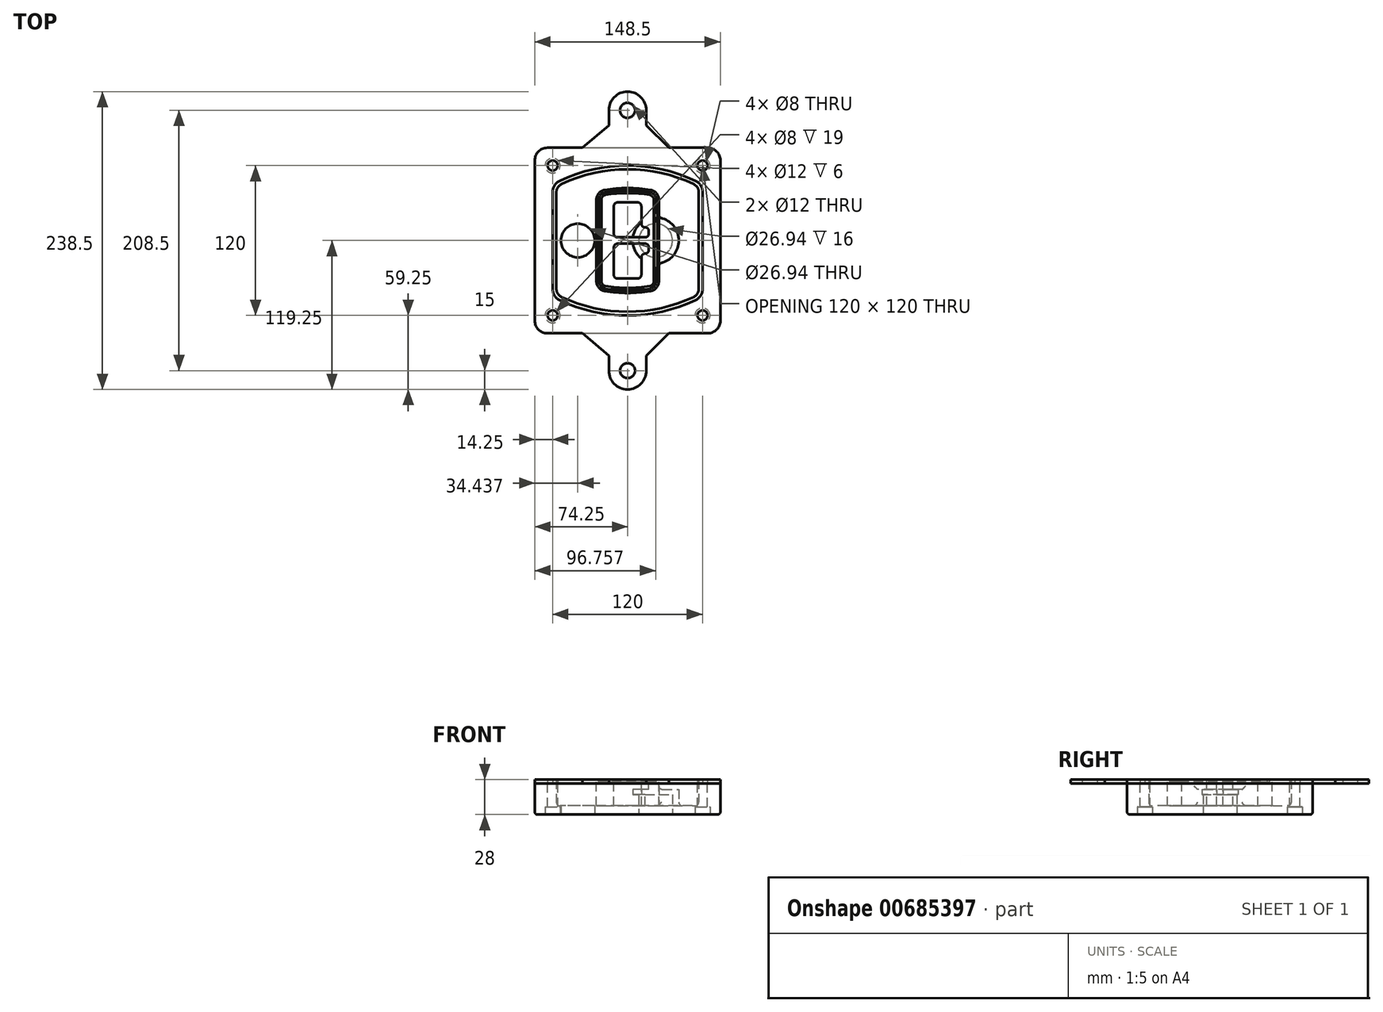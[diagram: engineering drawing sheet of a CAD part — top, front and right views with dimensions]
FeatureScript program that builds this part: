
annotation { "Feature Type Name" : "Feature", "Feature Type Description" : "" }
export const myFeature = defineFeature(function(context is Context, id is Id, definition is map)
    precondition{}
    {
        {
            var Q0;
            Q0=qCreatedBy(makeId("Top.planeOp"),FACE);
            var sketch = newSketch(context, id + "F0", { "sketchPlane" : qUnion([Q0])});
            skPoint(sketch, "E0.rect.middle", {"position": v(0, 0) * mm});
            skLineSegment(sketch, "E1.bottom", {"start": v(-64.25, -74.25) * mm, "end": v(64.25, -74.25) * mm});
            skLineSegment(sketch, "E1.top", {"start": v(-64.25, 74.25) * mm, "end": v(64.25, 74.25) * mm});
            skLineSegment(sketch, "E1.left", {"start": v(-74.25, -64.25) * mm, "end": v(-74.25, 64.25) * mm});
            skLineSegment(sketch, "E1.right", {"start": v(74.25, -64.25) * mm, "end": v(74.25, 64.25) * mm});
            skLineSegment(sketch, "E2", {"start": v(-74.25, 74.25) * mm, "end": v(74.25, -74.25) * mm, "construction": true});
            skLineSegment(sketch, "E3", {"start": v(74.25, 74.25) * mm, "end": v(-74.25, -74.25) * mm, "construction": true});
            skCircle(sketch, "E4", {"center": v(-60, 60) * mm, "radius": 4 * mm});
            skCircle(sketch, "E5", {"center": v(60, 60) * mm, "radius": 4 * mm});
            skCircle(sketch, "E6", {"center": v(60, -60) * mm, "radius": 4 * mm});
            skCircle(sketch, "E7", {"center": v(-60, -60) * mm, "radius": 4 * mm});
            skLineSegment(sketch, "E8", {"start": v(-60, 60) * mm, "end": v(60, 60) * mm, "construction": true});
            skLineSegment(sketch, "E9", {"start": v(60, 60) * mm, "end": v(60, -60) * mm, "construction": true});
            skLineSegment(sketch, "E10", {"start": v(60, -60) * mm, "end": v(-60, -60) * mm, "construction": true});
            skLineSegment(sketch, "E11", {"start": v(-60, -60) * mm, "end": v(-60, 60) * mm, "construction": true});
            skLineSegment(sketch, "E12", {"start": v(-60, 38.83) * mm, "end": v(-60, -38.83) * mm});
            skLineSegment(sketch, "E13", {"start": v(60, 38.83) * mm, "end": v(60, -38.83) * mm});
            skArc(sketch, "E14", {"start": v(54.26, 47.88) * mm, "mid": v(0, 60) * mm, "end": v(-54.26, 47.88) * mm});
            skArc(sketch, "E15", {"start": v(-54.26, -47.88) * mm, "mid": v(0, -60) * mm, "end": v(54.26, -47.88) * mm});
            skLineSegment(sketch, "E16", {"start": v(-60, 0) * mm, "end": v(60, 0) * mm, "construction": true});
            skPoint(sketch, "E17.visualSharp", {"position": v(-60, -45) * mm});
            skArc(sketch, "E17.filletArc", {"start": v(-60, -38.83) * mm, "mid": v(-58.44, -44.2) * mm, "end": v(-54.26, -47.88) * mm});
            skPoint(sketch, "E18.visualSharp", {"position": v(-60, 45) * mm});
            skArc(sketch, "E18.filletArc", {"start": v(-54.26, 47.88) * mm, "mid": v(-58.44, 44.2) * mm, "end": v(-60, 38.83) * mm});
            skPoint(sketch, "E19.visualSharp", {"position": v(60, 45) * mm});
            skArc(sketch, "E19.filletArc", {"start": v(60, 38.83) * mm, "mid": v(58.44, 44.2) * mm, "end": v(54.26, 47.88) * mm});
            skPoint(sketch, "E20.visualSharp", {"position": v(60, -45) * mm});
            skArc(sketch, "E20.filletArc", {"start": v(54.26, -47.88) * mm, "mid": v(58.44, -44.2) * mm, "end": v(60, -38.83) * mm});
            skPoint(sketch, "E21.visualSharp", {"position": v(-74.25, 74.25) * mm});
            skArc(sketch, "E21.filletArc", {"start": v(-64.25, 74.25) * mm, "mid": v(-71.32, 71.32) * mm, "end": v(-74.25, 64.25) * mm});
            skPoint(sketch, "E22.visualSharp", {"position": v(74.25, 74.25) * mm});
            skArc(sketch, "E22.filletArc", {"start": v(74.25, 64.25) * mm, "mid": v(71.32, 71.32) * mm, "end": v(64.25, 74.25) * mm});
            skPoint(sketch, "E23.visualSharp", {"position": v(74.25, -74.25) * mm});
            skArc(sketch, "E23.filletArc", {"start": v(64.25, -74.25) * mm, "mid": v(71.32, -71.32) * mm, "end": v(74.25, -64.25) * mm});
            skPoint(sketch, "E24.visualSharp", {"position": v(-74.25, -74.25) * mm});
            skArc(sketch, "E24.filletArc", {"start": v(-74.25, -64.25) * mm, "mid": v(-71.32, -71.32) * mm, "end": v(-64.25, -74.25) * mm});
            skArc(sketch, "E25.0", {"start": v(57, 38.83) * mm, "mid": v(55.9, 42.58) * mm, "end": v(52.98, 45.17) * mm});
            skLineSegment(sketch, "E25.1", {"start": v(57, 38.83) * mm, "end": v(57, -38.83) * mm});
            skArc(sketch, "E25.2", {"start": v(52.98, -45.17) * mm, "mid": v(55.9, -42.58) * mm, "end": v(57, -38.83) * mm});
            skArc(sketch, "E25.3", {"start": v(-52.98, -45.17) * mm, "mid": v(0, -57) * mm, "end": v(52.98, -45.17) * mm});
            skArc(sketch, "E25.4", {"start": v(-57, -38.83) * mm, "mid": v(-55.9, -42.58) * mm, "end": v(-52.98, -45.17) * mm});
            skArc(sketch, "E25.5", {"start": v(52.98, 45.17) * mm, "mid": v(0, 57) * mm, "end": v(-52.98, 45.17) * mm});
            skLineSegment(sketch, "E25.6", {"start": v(-57, 38.83) * mm, "end": v(-57, -38.83) * mm});
            skArc(sketch, "E25.7", {"start": v(-52.98, 45.17) * mm, "mid": v(-55.9, 42.58) * mm, "end": v(-57, 38.83) * mm});
            skArc(sketch, "E26.0", {"start": v(-55.96, 51.5) * mm, "mid": v(-61.82, 46.33) * mm, "end": v(-64, 38.83) * mm});
            skArc(sketch, "E26.1", {"start": v(55.96, 51.5) * mm, "mid": v(0, 64) * mm, "end": v(-55.96, 51.5) * mm});
            skArc(sketch, "E26.2", {"start": v(64, 38.83) * mm, "mid": v(61.82, 46.33) * mm, "end": v(55.96, 51.5) * mm});
            skLineSegment(sketch, "E26.3", {"start": v(64, 38.83) * mm, "end": v(64, -38.83) * mm});
            skArc(sketch, "E26.4", {"start": v(55.96, -51.5) * mm, "mid": v(61.82, -46.33) * mm, "end": v(64, -38.83) * mm});
            skLineSegment(sketch, "E26.5", {"start": v(-64, 38.83) * mm, "end": v(-64, -38.83) * mm});
            skArc(sketch, "E26.6", {"start": v(-55.96, -51.5) * mm, "mid": v(0, -64) * mm, "end": v(55.96, -51.5) * mm});
            skArc(sketch, "E26.7", {"start": v(-64, -38.83) * mm, "mid": v(-61.82, -46.33) * mm, "end": v(-55.96, -51.5) * mm});
            skSolve(sketch);
        }
        {
            var Q0;
            Q0=makeQuery(id+"F0.imprint","IMPRINT",FACE,{"disambiguationData":[TD([[makeQuery(id+"F0.imprint","IMPRINT",EDGE,{"derivedFrom":sQuery(id+"F0.wireOp",EDGE,"E1.bottom")}),1.0]])]});
            var Q1;
            Q1=makeQuery(id+"F0.imprint","IMPRINT",FACE,{"disambiguationData":[TD([[makeQuery(id+"F0.imprint","IMPRINT",EDGE,{"derivedFrom":sQuery(id+"F0.wireOp",EDGE,"E12")}),1.0]])]});
            var Q2;
            Q2=makeQuery(id+"F0.imprint","IMPRINT",FACE,{"disambiguationData":[TD([[makeQuery(id+"F0.imprint","IMPRINT",EDGE,{"derivedFrom":sQuery(id+"F0.wireOp",EDGE,"E25.0")}),1.0]])]});
            var Q3;
            Q3=makeQuery(id+"F0.imprint","IMPRINT",FACE,{"disambiguationData":[TD([[makeQuery(id+"F0.imprint","IMPRINT",EDGE,{"derivedFrom":sQuery(id+"F0.wireOp",EDGE,"E12")}),-1.0]])]});
            extrude(context, id + "F1", {"entities" : qUnion([Q0, Q1, Q2, Q3]), "oppositeDirection" : true, "depth" : 25 * mm});
        }
        {
            var Q0;
            Q0=makeQuery(id+"F0.imprint","IMPRINT",FACE,{"disambiguationData":[TD([[makeQuery(id+"F0.imprint","IMPRINT",EDGE,{"derivedFrom":sQuery(id+"F0.wireOp",EDGE,"E12")}),1.0]])]});
            extrude(context, id + "F2", {"entities" : qUnion([Q0]), "operationType" : NewBodyOperationType.ADD, "depth" : 3 * mm});
        }
        {
            var Q0;
            Q0=makeQuery(id+"F0.imprint","IMPRINT",FACE,{"disambiguationData":[TD([[makeQuery(id+"F0.imprint","IMPRINT",EDGE,{"derivedFrom":sQuery(id+"F0.wireOp",EDGE,"E25.0")}),1.0]])]});
            extrude(context, id + "F3", {"entities" : qUnion([Q0]), "operationType" : NewBodyOperationType.REMOVE, "oppositeDirection" : true, "depth" : 18 * mm});
        }
        {
            var Q0;
            Q0=makeQuery(id+"F2.opExtrude","CAP_FACE",FACE,{"disambiguationData":[OSD([sQuery(id+"F0.wireOp",EDGE,"E12"),sQuery(id+"F0.wireOp",EDGE,"E13"),sQuery(id+"F0.wireOp",EDGE,"E14"),sQuery(id+"F0.wireOp",EDGE,"E15"),sQuery(id+"F0.wireOp",EDGE,"E17.filletArc"),sQuery(id+"F0.wireOp",EDGE,"E18.filletArc"),sQuery(id+"F0.wireOp",EDGE,"E19.filletArc"),sQuery(id+"F0.wireOp",EDGE,"E20.filletArc"),sQuery(id+"F0.wireOp",EDGE,"E25.0"),sQuery(id+"F0.wireOp",EDGE,"E25.1"),sQuery(id+"F0.wireOp",EDGE,"E25.2"),sQuery(id+"F0.wireOp",EDGE,"E25.3"),sQuery(id+"F0.wireOp",EDGE,"E25.4"),sQuery(id+"F0.wireOp",EDGE,"E25.5"),sQuery(id+"F0.wireOp",EDGE,"E25.6"),sQuery(id+"F0.wireOp",EDGE,"E25.7")])],"isStart":false});
            var sketch = newSketch(context, id + "F4", { "sketchPlane" : qUnion([Q0])});
            skArc(sketch, "E27.0", {"start": v(-18.34, -40.45) * mm, "mid": v(0, -42) * mm, "end": v(18.34, -40.45) * mm});
            skArc(sketch, "E28.0", {"start": v(18.34, 40.45) * mm, "mid": v(0, 42) * mm, "end": v(-18.34, 40.45) * mm});
            skLineSegment(sketch, "E29", {"start": v(-25, 32.57) * mm, "end": v(-25, -32.57) * mm});
            skLineSegment(sketch, "E30", {"start": v(25, 32.57) * mm, "end": v(25, -32.57) * mm});
            skLineSegment(sketch, "E31", {"start": v(-25, 39.1) * mm, "end": v(25, 39.1) * mm, "construction": true});
            skLineSegment(sketch, "E32", {"start": v(-25, -39.1) * mm, "end": v(25, -39.1) * mm, "construction": true});
            skPoint(sketch, "E33.visualSharp", {"position": v(-25, 39.1) * mm});
            skArc(sketch, "E33.filletArc", {"start": v(-18.34, 40.45) * mm, "mid": v(-23.11, 37.73) * mm, "end": v(-25, 32.57) * mm});
            skPoint(sketch, "E34.visualSharp", {"position": v(25, 39.1) * mm});
            skArc(sketch, "E34.filletArc", {"start": v(25, 32.57) * mm, "mid": v(23.11, 37.73) * mm, "end": v(18.34, 40.45) * mm});
            skPoint(sketch, "E35.visualSharp", {"position": v(25, -39.1) * mm});
            skArc(sketch, "E35.filletArc", {"start": v(18.34, -40.45) * mm, "mid": v(23.11, -37.73) * mm, "end": v(25, -32.57) * mm});
            skPoint(sketch, "E36.visualSharp", {"position": v(-25, -39.1) * mm});
            skArc(sketch, "E36.filletArc", {"start": v(-25, -32.57) * mm, "mid": v(-23.11, -37.73) * mm, "end": v(-18.34, -40.45) * mm});
            skArc(sketch, "E37.0", {"start": v(52.98, 45.17) * mm, "mid": v(0, 57) * mm, "end": v(-52.98, 45.17) * mm});
            skArc(sketch, "E37.1", {"start": v(-52.98, 45.17) * mm, "mid": v(-55.9, 42.58) * mm, "end": v(-57, 38.83) * mm});
            skLineSegment(sketch, "E37.2", {"start": v(-57, 38.83) * mm, "end": v(-57, -38.83) * mm});
            skArc(sketch, "E37.3", {"start": v(-57, -38.83) * mm, "mid": v(-55.9, -42.58) * mm, "end": v(-52.98, -45.17) * mm});
            skArc(sketch, "E37.4", {"start": v(-52.98, -45.17) * mm, "mid": v(0, -57) * mm, "end": v(52.98, -45.17) * mm});
            skArc(sketch, "E37.5", {"start": v(52.98, -45.17) * mm, "mid": v(55.9, -42.58) * mm, "end": v(57, -38.83) * mm});
            skLineSegment(sketch, "E37.6", {"start": v(57, 38.83) * mm, "end": v(57, -38.83) * mm});
            skArc(sketch, "E37.7", {"start": v(57, 38.83) * mm, "mid": v(55.9, 42.58) * mm, "end": v(52.98, 45.17) * mm});
            skLineSegment(sketch, "E38.0", {"start": v(23, 32.57) * mm, "end": v(23, -32.57) * mm});
            skArc(sketch, "E38.1", {"start": v(18, -38.48) * mm, "mid": v(21.58, -36.44) * mm, "end": v(23, -32.57) * mm});
            skArc(sketch, "E38.2", {"start": v(-18, -38.48) * mm, "mid": v(0, -40) * mm, "end": v(18, -38.48) * mm});
            skArc(sketch, "E38.3", {"start": v(-23, -32.57) * mm, "mid": v(-21.58, -36.44) * mm, "end": v(-18, -38.48) * mm});
            skLineSegment(sketch, "E38.4", {"start": v(-23, 32.57) * mm, "end": v(-23, -32.57) * mm});
            skArc(sketch, "E38.5", {"start": v(23, 32.57) * mm, "mid": v(21.58, 36.44) * mm, "end": v(18, 38.48) * mm});
            skArc(sketch, "E38.6", {"start": v(-18, 38.48) * mm, "mid": v(-21.58, 36.44) * mm, "end": v(-23, 32.57) * mm});
            skArc(sketch, "E38.7", {"start": v(18, 38.48) * mm, "mid": v(0, 40) * mm, "end": v(-18, 38.48) * mm});
            skArc(sketch, "E39.0", {"start": v(21, 32.57) * mm, "mid": v(20.06, 35.15) * mm, "end": v(17.67, 36.5) * mm});
            skLineSegment(sketch, "E39.1", {"start": v(21, 32.57) * mm, "end": v(21, -32.57) * mm});
            skArc(sketch, "E39.2", {"start": v(17.67, -36.5) * mm, "mid": v(20.06, -35.15) * mm, "end": v(21, -32.57) * mm});
            skArc(sketch, "E39.3", {"start": v(-17.67, -36.5) * mm, "mid": v(0, -38) * mm, "end": v(17.67, -36.5) * mm});
            skArc(sketch, "E39.4", {"start": v(-21, -32.57) * mm, "mid": v(-20.06, -35.15) * mm, "end": v(-17.67, -36.5) * mm});
            skArc(sketch, "E39.5", {"start": v(17.67, 36.5) * mm, "mid": v(0, 38) * mm, "end": v(-17.67, 36.5) * mm});
            skLineSegment(sketch, "E39.6", {"start": v(-21, 32.57) * mm, "end": v(-21, -32.57) * mm});
            skArc(sketch, "E39.7", {"start": v(-17.67, 36.5) * mm, "mid": v(-20.06, 35.15) * mm, "end": v(-21, 32.57) * mm});
            skLineSegment(sketch, "E40", {"start": v(-25, 0) * mm, "end": v(25, 0) * mm, "construction": true});
            skLineSegment(sketch, "E41", {"start": v(-11, 5.5) * mm, "end": v(-11, 27.5) * mm});
            skLineSegment(sketch, "E42", {"start": v(-8, 30.5) * mm, "end": v(8, 30.5) * mm});
            skLineSegment(sketch, "E43", {"start": v(11, 27.5) * mm, "end": v(11, 13.5) * mm});
            skLineSegment(sketch, "E44", {"start": v(14, 10.5) * mm, "end": v(14, 10.5) * mm});
            skLineSegment(sketch, "E45", {"start": v(17, 7.5) * mm, "end": v(17, 5.5) * mm});
            skLineSegment(sketch, "E46", {"start": v(14, 2.5) * mm, "end": v(-8, 2.5) * mm});
            skPoint(sketch, "E47.visualSharp", {"position": v(-11, 30.5) * mm});
            skArc(sketch, "E47.filletArc", {"start": v(-8, 30.5) * mm, "mid": v(-10.12, 29.62) * mm, "end": v(-11, 27.5) * mm});
            skPoint(sketch, "E48.visualSharp", {"position": v(11, 30.5) * mm});
            skArc(sketch, "E48.filletArc", {"start": v(11, 27.5) * mm, "mid": v(10.12, 29.62) * mm, "end": v(8, 30.5) * mm});
            skPoint(sketch, "E49.visualSharp", {"position": v(11, 10.5) * mm});
            skArc(sketch, "E49.filletArc", {"start": v(11, 13.5) * mm, "mid": v(11.88, 11.38) * mm, "end": v(14, 10.5) * mm});
            skPoint(sketch, "E50.visualSharp", {"position": v(17, 10.5) * mm});
            skArc(sketch, "E50.filletArc", {"start": v(17, 7.5) * mm, "mid": v(16.12, 9.62) * mm, "end": v(14, 10.5) * mm});
            skPoint(sketch, "E51.visualSharp", {"position": v(17, 2.5) * mm});
            skArc(sketch, "E51.filletArc", {"start": v(14, 2.5) * mm, "mid": v(16.12, 3.38) * mm, "end": v(17, 5.5) * mm});
            skPoint(sketch, "E52.visualSharp", {"position": v(-11, 2.5) * mm});
            skArc(sketch, "E52.filletArc", {"start": v(-11, 5.5) * mm, "mid": v(-10.12, 3.38) * mm, "end": v(-8, 2.5) * mm});
            skLineSegment(sketch, "E53.0.MirrorCS", {"start": v(14, -2.5) * mm, "end": v(-8, -2.5) * mm});
            skArc(sketch, "E54.0.MirrorCS", {"start": v(-11, -5.5) * mm, "mid": v(-10.12, -3.38) * mm, "end": v(-8, -2.5) * mm});
            skLineSegment(sketch, "E55.0.MirrorCS", {"start": v(-11, -5.5) * mm, "end": v(-11, -27.5) * mm});
            skArc(sketch, "E56.0.MirrorCS", {"start": v(-8, -30.5) * mm, "mid": v(-10.12, -29.62) * mm, "end": v(-11, -27.5) * mm});
            skLineSegment(sketch, "E57.0.MirrorCS", {"start": v(-8, -30.5) * mm, "end": v(8, -30.5) * mm});
            skArc(sketch, "E58.0.MirrorCS", {"start": v(11, -27.5) * mm, "mid": v(10.12, -29.62) * mm, "end": v(8, -30.5) * mm});
            skLineSegment(sketch, "E59.0.MirrorCS", {"start": v(11, -27.5) * mm, "end": v(11, -13.5) * mm});
            skArc(sketch, "E60.0.MirrorCS", {"start": v(11, -13.5) * mm, "mid": v(11.88, -11.38) * mm, "end": v(14, -10.5) * mm});
            skArc(sketch, "E61.0.MirrorCS", {"start": v(17, -7.5) * mm, "mid": v(16.12, -9.62) * mm, "end": v(14, -10.5) * mm});
            skLineSegment(sketch, "E62.0.MirrorCS", {"start": v(17, -7.5) * mm, "end": v(17, -5.5) * mm});
            skArc(sketch, "E63.0.MirrorCS", {"start": v(14, -2.5) * mm, "mid": v(16.12, -3.38) * mm, "end": v(17, -5.5) * mm});
            skSolve(sketch);
        }
        {
            var Q0;
            Q0=makeQuery(id+"F4.imprint","IMPRINT",FACE,{"disambiguationData":[TD([[makeQuery(id+"F4.imprint","IMPRINT",EDGE,{"derivedFrom":sQuery(id+"F4.wireOp",EDGE,"E27.0")}),1.0]])]});
            var Q1;
            Q1=makeQuery(id+"F4.imprint","IMPRINT",FACE,{"disambiguationData":[TD([[makeQuery(id+"F4.imprint","IMPRINT",EDGE,{"derivedFrom":sQuery(id+"F4.wireOp",EDGE,"E38.0")}),-1.0]])]});
            var Q2;
            Q2=makeQuery(id+"F4.imprint","IMPRINT",FACE,{"disambiguationData":[TD([[makeQuery(id+"F4.imprint","IMPRINT",EDGE,{"derivedFrom":sQuery(id+"F4.wireOp",EDGE,"E39.0")}),1.0]])]});
            extrude(context, id + "F5", {"entities" : qUnion([Q0, Q1, Q2]), "operationType" : NewBodyOperationType.ADD, "endBound" : BoundingType.UP_TO_NEXT, "oppositeDirection" : true, "depth" : 25 * mm});
        }
        {
            var Q0;
            Q0=makeQuery(id+"F4.imprint","IMPRINT",FACE,{"disambiguationData":[TD([[makeQuery(id+"F4.imprint","IMPRINT",EDGE,{"derivedFrom":sQuery(id+"F4.wireOp",EDGE,"E38.0")}),-1.0]])]});
            extrude(context, id + "F6", {"entities" : qUnion([Q0]), "operationType" : NewBodyOperationType.REMOVE, "oppositeDirection" : true, "depth" : 2 * mm});
        }
        {
            var Q0;
            Q0=makeQuery(id+"F1.opExtrude","CAP_FACE",FACE,{"disambiguationData":[OSD([sQuery(id+"F0.wireOp",EDGE,"E1.bottom"),sQuery(id+"F0.wireOp",EDGE,"E1.top"),sQuery(id+"F0.wireOp",EDGE,"E1.left"),sQuery(id+"F0.wireOp",EDGE,"E1.right"),sQuery(id+"F0.wireOp",EDGE,"E4"),sQuery(id+"F0.wireOp",EDGE,"E5"),sQuery(id+"F0.wireOp",EDGE,"E6"),sQuery(id+"F0.wireOp",EDGE,"E7"),sQuery(id+"F0.wireOp",EDGE,"E21.filletArc"),sQuery(id+"F0.wireOp",EDGE,"E22.filletArc"),sQuery(id+"F0.wireOp",EDGE,"E23.filletArc"),sQuery(id+"F0.wireOp",EDGE,"E24.filletArc")])],"isStart":false});
            var sketch = newSketch(context, id + "F7", { "sketchPlane" : qUnion([Q0])});
            skCircle(sketch, "E64", {"center": v(22.5, 0) * mm, "radius": 13.47 * mm});
            skCircle(sketch, "E65", {"center": v(-39.81, 0) * mm, "radius": 13.47 * mm});
            skLineSegment(sketch, "E66", {"start": v(74.25, 0) * mm, "end": v(-74.25, 0) * mm});
            skCircle(sketch, "E67", {"center": v(22.5, 0) * mm, "radius": 18.47 * mm});
            skCircle(sketch, "E68", {"center": v(60, -60) * mm, "radius": 6 * mm});
            skCircle(sketch, "E69", {"center": v(-60, -60) * mm, "radius": 6 * mm});
            skCircle(sketch, "E70", {"center": v(-60, 60) * mm, "radius": 6 * mm});
            skCircle(sketch, "E71", {"center": v(60, 60) * mm, "radius": 6 * mm});
            skSolve(sketch);
        }
        {
            var Q0;
            {var subQ1=sQuery(id+"F7.wireOp",EDGE,"E66");var subQ4=sQuery(id+"F7.wireOp",EDGE,"E64");var subQ6=makeQuery(id+"F7.imprint","INTERSECT",VERTEX,{"disambiguationData":[OD(0.0)],"derivedFrom":[subQ4,subQ1]});Q0=makeQuery(id+"F7.imprint","IMPRINT",FACE,{"disambiguationData":[TD([[makeQuery(id+"F7.imprint","IMPRINT",EDGE,{"disambiguationData":[TD([[subQ6,-1.0]])],"derivedFrom":subQ4}),-1.0]])]});}
            var Q1;
            {var subQ0=sQuery(id+"F7.wireOp",EDGE,"E66");var subQ1=sQuery(id+"F7.wireOp",EDGE,"E64");var subQ3=makeQuery(id+"F7.imprint","INTERSECT",VERTEX,{"disambiguationData":[OD(0.0)],"derivedFrom":[subQ1,subQ0]});Q1=makeQuery(id+"F7.imprint","IMPRINT",FACE,{"disambiguationData":[TD([[makeQuery(id+"F7.imprint","IMPRINT",EDGE,{"disambiguationData":[TD([[subQ3,-1.0]])],"derivedFrom":subQ1}),1.0]])]});}
            var Q2;
            {var subQ0=sQuery(id+"F7.wireOp",EDGE,"E66");var subQ1=sQuery(id+"F7.wireOp",EDGE,"E64");var subQ3=makeQuery(id+"F7.imprint","INTERSECT",VERTEX,{"disambiguationData":[OD(0.0)],"derivedFrom":[subQ1,subQ0]});Q2=makeQuery(id+"F7.imprint","IMPRINT",FACE,{"disambiguationData":[TD([[makeQuery(id+"F7.imprint","IMPRINT",EDGE,{"disambiguationData":[TD([[subQ3,1.0]])],"derivedFrom":subQ1}),1.0]])]});}
            var Q3;
            {var subQ1=sQuery(id+"F7.wireOp",EDGE,"E66");var subQ4=sQuery(id+"F7.wireOp",EDGE,"E64");var subQ6=makeQuery(id+"F7.imprint","INTERSECT",VERTEX,{"disambiguationData":[OD(0.0)],"derivedFrom":[subQ4,subQ1]});Q3=makeQuery(id+"F7.imprint","IMPRINT",FACE,{"disambiguationData":[TD([[makeQuery(id+"F7.imprint","IMPRINT",EDGE,{"disambiguationData":[TD([[subQ6,1.0]])],"derivedFrom":subQ4}),-1.0]])]});}
            extrude(context, id + "F8", {"entities" : qUnion([Q0, Q1, Q2, Q3]), "operationType" : NewBodyOperationType.ADD, "oppositeDirection" : true, "depth" : 20 * mm});
        }
        {
            var Q0;
            {var subQ0=sQuery(id+"F7.wireOp",EDGE,"E66");var subQ1=sQuery(id+"F7.wireOp",EDGE,"E64");var subQ3=makeQuery(id+"F7.imprint","INTERSECT",VERTEX,{"disambiguationData":[OD(0.0)],"derivedFrom":[subQ1,subQ0]});Q0=makeQuery(id+"F7.imprint","IMPRINT",FACE,{"disambiguationData":[TD([[makeQuery(id+"F7.imprint","IMPRINT",EDGE,{"disambiguationData":[TD([[subQ3,-1.0]])],"derivedFrom":subQ1}),1.0]])]});}
            var Q1;
            {var subQ0=sQuery(id+"F7.wireOp",EDGE,"E66");var subQ1=sQuery(id+"F7.wireOp",EDGE,"E64");var subQ3=makeQuery(id+"F7.imprint","INTERSECT",VERTEX,{"disambiguationData":[OD(0.0)],"derivedFrom":[subQ1,subQ0]});Q1=makeQuery(id+"F7.imprint","IMPRINT",FACE,{"disambiguationData":[TD([[makeQuery(id+"F7.imprint","IMPRINT",EDGE,{"disambiguationData":[TD([[subQ3,1.0]])],"derivedFrom":subQ1}),1.0]])]});}
            extrude(context, id + "F9", {"entities" : qUnion([Q0, Q1]), "operationType" : NewBodyOperationType.REMOVE, "oppositeDirection" : true, "depth" : 16 * mm});
        }
        {
            var Q0;
            {var subQ0=sQuery(id+"F7.wireOp",EDGE,"E66");var subQ1=sQuery(id+"F7.wireOp",EDGE,"E65");var subQ3=makeQuery(id+"F7.imprint","INTERSECT",VERTEX,{"disambiguationData":[OD(0.0)],"derivedFrom":[subQ1,subQ0]});Q0=makeQuery(id+"F7.imprint","IMPRINT",FACE,{"disambiguationData":[TD([[makeQuery(id+"F7.imprint","IMPRINT",EDGE,{"disambiguationData":[TD([[subQ3,-1.0]])],"derivedFrom":subQ1}),1.0]])]});}
            var Q1;
            {var subQ0=sQuery(id+"F7.wireOp",EDGE,"E66");var subQ1=sQuery(id+"F7.wireOp",EDGE,"E65");var subQ3=makeQuery(id+"F7.imprint","INTERSECT",VERTEX,{"disambiguationData":[OD(0.0)],"derivedFrom":[subQ1,subQ0]});Q1=makeQuery(id+"F7.imprint","IMPRINT",FACE,{"disambiguationData":[TD([[makeQuery(id+"F7.imprint","IMPRINT",EDGE,{"disambiguationData":[TD([[subQ3,1.0]])],"derivedFrom":subQ1}),1.0]])]});}
            extrude(context, id + "F10", {"entities" : qUnion([Q0, Q1]), "operationType" : NewBodyOperationType.REMOVE, "oppositeDirection" : true, "depth" : 25 * mm});
        }
        {
            var Q0;
            Q0=makeQuery(id+"F7.imprint","IMPRINT",FACE,{"disambiguationData":[TD([[makeQuery(id+"F7.imprint","IMPRINT",EDGE,{"derivedFrom":sQuery(id+"F7.wireOp",EDGE,"E68")}),1.0]])]});
            var Q1;
            Q1=makeQuery(id+"F7.imprint","IMPRINT",FACE,{"disambiguationData":[TD([[makeQuery(id+"F7.imprint","IMPRINT",EDGE,{"derivedFrom":makeQuery(id+"F1.opExtrude","CAP_EDGE",EDGE,{"disambiguationData":[OSD([sQuery(id+"F0.wireOp",EDGE,"E5")])],"isStart":false})}),-1.0]])]});
            var Q2;
            Q2=makeQuery(id+"F7.imprint","IMPRINT",FACE,{"disambiguationData":[TD([[makeQuery(id+"F7.imprint","IMPRINT",EDGE,{"derivedFrom":sQuery(id+"F7.wireOp",EDGE,"E69")}),1.0]])]});
            var Q3;
            Q3=makeQuery(id+"F7.imprint","IMPRINT",FACE,{"disambiguationData":[TD([[makeQuery(id+"F7.imprint","IMPRINT",EDGE,{"derivedFrom":makeQuery(id+"F1.opExtrude","CAP_EDGE",EDGE,{"disambiguationData":[OSD([sQuery(id+"F0.wireOp",EDGE,"E4")])],"isStart":false})}),-1.0]])]});
            var Q4;
            Q4=makeQuery(id+"F7.imprint","IMPRINT",FACE,{"disambiguationData":[TD([[makeQuery(id+"F7.imprint","IMPRINT",EDGE,{"derivedFrom":sQuery(id+"F7.wireOp",EDGE,"E70")}),1.0]])]});
            var Q5;
            Q5=makeQuery(id+"F7.imprint","IMPRINT",FACE,{"disambiguationData":[TD([[makeQuery(id+"F7.imprint","IMPRINT",EDGE,{"derivedFrom":makeQuery(id+"F1.opExtrude","CAP_EDGE",EDGE,{"disambiguationData":[OSD([sQuery(id+"F0.wireOp",EDGE,"E7")])],"isStart":false})}),-1.0]])]});
            var Q6;
            Q6=makeQuery(id+"F7.imprint","IMPRINT",FACE,{"disambiguationData":[TD([[makeQuery(id+"F7.imprint","IMPRINT",EDGE,{"derivedFrom":sQuery(id+"F7.wireOp",EDGE,"E71")}),1.0]])]});
            var Q7;
            Q7=makeQuery(id+"F7.imprint","IMPRINT",FACE,{"disambiguationData":[TD([[makeQuery(id+"F7.imprint","IMPRINT",EDGE,{"derivedFrom":makeQuery(id+"F1.opExtrude","CAP_EDGE",EDGE,{"disambiguationData":[OSD([sQuery(id+"F0.wireOp",EDGE,"E6")])],"isStart":false})}),-1.0]])]});
            extrude(context, id + "F11", {"entities" : qUnion([Q0, Q1, Q2, Q3, Q4, Q5, Q6, Q7]), "operationType" : NewBodyOperationType.REMOVE, "oppositeDirection" : true, "depth" : 6 * mm});
        }
        {
            var Q0;
            Q0=makeQuery(id+"F9.boolean.opBoolean","COPY",FACE,{"derivedFrom":makeQuery(id+"F9.opExtrude","CAP_FACE",FACE,{"disambiguationData":[OSD([sQuery(id+"F7.wireOp",EDGE,"E64")])],"isStart":false})});
            var sketch = newSketch(context, id + "F12", { "sketchPlane" : qUnion([Q0])});
            skArc(sketch, "E72.0", {"start": v(11, 14.45) * mm, "mid": v(6.45, 9.13) * mm, "end": v(4.2, 2.5) * mm});
            skArc(sketch, "E72.1", {"start": v(4.2, -2.5) * mm, "mid": v(6.45, -9.13) * mm, "end": v(11, -14.45) * mm});
            skLineSegment(sketch, "E73", {"start": v(4.2, -2.5) * mm, "end": v(14, -2.5) * mm});
            skLineSegment(sketch, "E74.0", {"start": v(14, 2.5) * mm, "end": v(4.2, 2.5) * mm});
            skArc(sketch, "E74.1", {"start": v(14, 2.5) * mm, "mid": v(16.12, 3.38) * mm, "end": v(17, 5.5) * mm});
            skLineSegment(sketch, "E74.2", {"start": v(17, 7.5) * mm, "end": v(17, 5.5) * mm});
            skArc(sketch, "E74.3", {"start": v(17, 7.5) * mm, "mid": v(16.12, 9.62) * mm, "end": v(14, 10.5) * mm});
            skArc(sketch, "E74.4", {"start": v(11, 13.5) * mm, "mid": v(11.88, 11.38) * mm, "end": v(14, 10.5) * mm});
            skLineSegment(sketch, "E74.5", {"start": v(11, 14.45) * mm, "end": v(11, 13.5) * mm});
            skLineSegment(sketch, "E74.7", {"start": v(14, -2.5) * mm, "end": v(4.2, -2.5) * mm});
            skArc(sketch, "E74.8", {"start": v(14, -2.5) * mm, "mid": v(16.12, -3.38) * mm, "end": v(17, -5.5) * mm});
            skLineSegment(sketch, "E74.9", {"start": v(17, -7.5) * mm, "end": v(17, -5.5) * mm});
            skArc(sketch, "E74.10", {"start": v(17, -7.5) * mm, "mid": v(16.12, -9.62) * mm, "end": v(14, -10.5) * mm});
            skArc(sketch, "E74.11", {"start": v(11, -13.5) * mm, "mid": v(11.88, -11.38) * mm, "end": v(14, -10.5) * mm});
            skLineSegment(sketch, "E74.12", {"start": v(11, -14.45) * mm, "end": v(11, -13.5) * mm});
            skPoint(sketch, "E75.orphan", {"position": v(11, -27.5) * mm});
            skPoint(sketch, "E76.orphan", {"position": v(-8, -2.5) * mm});
            skPoint(sketch, "E77.orphan", {"position": v(-8, 2.5) * mm});
            skPoint(sketch, "E78.orphan", {"position": v(11, 27.5) * mm});
            skSolve(sketch);
        }
        {
            var Q0;
            {var subQ7=sQuery(id+"F12.wireOp",EDGE,"E72.0");var subQ14=sQuery(id+"F12.wireOp",EDGE,"E72.1");var subQ16=sQuery(id+"F12.wireOp",EDGE,"E74.1");var subQ18=sQuery(id+"F12.wireOp",EDGE,"E74.8");Q0=qUnion([makeQuery(id+"F12.imprint","IMPRINT",FACE,{"disambiguationData":[TD([[makeQuery(id+"F12.imprint","IMPRINT",EDGE,{"derivedFrom":subQ7}),1.0]])]}),makeQuery(id+"F12.imprint","IMPRINT",FACE,{"disambiguationData":[TD([[makeQuery(id+"F12.imprint","IMPRINT",EDGE,{"derivedFrom":subQ14}),1.0]])]}),makeQuery(id+"F12.imprint","IMPRINT",FACE,{"disambiguationData":[TD([[makeQuery(id+"F12.imprint","IMPRINT",EDGE,{"derivedFrom":subQ16}),1.0]])]}),makeQuery(id+"F12.imprint","IMPRINT",FACE,{"disambiguationData":[TD([[makeQuery(id+"F12.imprint","IMPRINT",EDGE,{"derivedFrom":subQ18}),-1.0]])]})]);}
            var Q1;
            Q1=makeQuery(id+"F5.boolean.opBoolean","SPLIT",FACE,{"disambiguationData":[TD([makeQuery(id+"F5.opExtrude","SWEPT_FACE",FACE,{"disambiguationData":[OSD([sQuery(id+"F4.wireOp",EDGE,"E41")])]})])],"derivedFrom":makeQuery(id+"F3.boolean.opBoolean","COPY",FACE,{"derivedFrom":makeQuery(id+"F3.opExtrude","CAP_FACE",FACE,{"disambiguationData":[OSD([sQuery(id+"F0.wireOp",EDGE,"E25.0"),sQuery(id+"F0.wireOp",EDGE,"E25.1"),sQuery(id+"F0.wireOp",EDGE,"E25.2"),sQuery(id+"F0.wireOp",EDGE,"E25.3"),sQuery(id+"F0.wireOp",EDGE,"E25.4"),sQuery(id+"F0.wireOp",EDGE,"E25.5"),sQuery(id+"F0.wireOp",EDGE,"E25.6"),sQuery(id+"F0.wireOp",EDGE,"E25.7")])],"isStart":false})})});
            extrude(context, id + "F13", {"entities" : qUnion([Q0]), "operationType" : NewBodyOperationType.REMOVE, "endBound" : BoundingType.UP_TO_SURFACE, "endBoundEntityFace" : qUnion([Q1]), "depth" : 25 * mm});
        }
        {
            var Q0;
            Q0=makeQuery(id+"F3.boolean.opBoolean","COPY",EDGE,{"derivedFrom":makeQuery(id+"F3.opExtrude","CAP_EDGE",EDGE,{"disambiguationData":[OSD([sQuery(id+"F0.wireOp",EDGE,"E25.6")])],"isStart":false})});
            var Q1;
            Q1=makeQuery(id+"F8.boolean.opBoolean","INTERSECT",EDGE,{"derivedFrom":[makeQuery(id+"F5.opExtrude","SWEPT_FACE",FACE,{"disambiguationData":[OSD([sQuery(id+"F4.wireOp",EDGE,"E30")])]}),makeQuery(id+"F8.opExtrude","CAP_FACE",FACE,{"disambiguationData":[OSD([sQuery(id+"F7.wireOp",EDGE,"E67")])],"isStart":false})]});
            var Q2;
            Q2=makeQuery(id+"F8.boolean.opBoolean","INTERSECT",EDGE,{"disambiguationData":[OD(1.0)],"derivedFrom":[makeQuery(id+"F5.opExtrude","SWEPT_FACE",FACE,{"disambiguationData":[OSD([sQuery(id+"F4.wireOp",EDGE,"E30")])]}),makeQuery(id+"F8.opExtrude","SWEPT_FACE",FACE,{"disambiguationData":[OSD([sQuery(id+"F7.wireOp",EDGE,"E67")])]})]});
            var Q3;
            {var subQ0=sQuery(id+"F4.wireOp",EDGE,"E30");Q3=makeQuery(id+"F8.boolean.opBoolean","SPLIT",EDGE,{"disambiguationData":[TD([makeQuery(id+"F5.opExtrude","SWEPT_FACE",FACE,{"disambiguationData":[OSD([sQuery(id+"F4.wireOp",EDGE,"E35.filletArc")])]})])],"derivedFrom":makeQuery(id+"F5.opExtrude","CAP_EDGE",EDGE,{"disambiguationData":[OSD([subQ0])],"isStart":false})});}
            var Q4;
            {var subQ0=sQuery(id+"F0.wireOp",EDGE,"E25.7");var subQ1=sQuery(id+"F0.wireOp",EDGE,"E25.1");var subQ2=sQuery(id+"F0.wireOp",EDGE,"E25.6");var subQ3=sQuery(id+"F0.wireOp",EDGE,"E25.5");var subQ4=sQuery(id+"F0.wireOp",EDGE,"E25.4");var subQ5=sQuery(id+"F0.wireOp",EDGE,"E25.0");var subQ6=sQuery(id+"F0.wireOp",EDGE,"E25.2");var subQ7=sQuery(id+"F0.wireOp",EDGE,"E25.3");Q4=makeQuery(id+"F8.boolean.opBoolean","INTERSECT",EDGE,{"derivedFrom":[makeQuery(id+"F5.boolean.opBoolean","SPLIT",FACE,{"disambiguationData":[TD([makeQuery(id+"F2.opExtrude","SWEPT_FACE",FACE,{"disambiguationData":[OSD([subQ5])]})])],"derivedFrom":makeQuery(id+"F3.boolean.opBoolean","COPY",FACE,{"derivedFrom":makeQuery(id+"F3.opExtrude","CAP_FACE",FACE,{"disambiguationData":[OSD([subQ5,subQ1,subQ6,subQ7,subQ4,subQ3,subQ2,subQ0])],"isStart":false})})}),makeQuery(id+"F8.opExtrude","SWEPT_FACE",FACE,{"disambiguationData":[OSD([sQuery(id+"F7.wireOp",EDGE,"E67")])]})]});}
            var Q5;
            Q5=makeQuery(id+"F8.boolean.opBoolean","INTERSECT",EDGE,{"disambiguationData":[OD(0.0)],"derivedFrom":[makeQuery(id+"F5.opExtrude","SWEPT_FACE",FACE,{"disambiguationData":[OSD([sQuery(id+"F4.wireOp",EDGE,"E30")])]}),makeQuery(id+"F8.opExtrude","SWEPT_FACE",FACE,{"disambiguationData":[OSD([sQuery(id+"F7.wireOp",EDGE,"E67")])]})]});
            fillet(context, id + "F14", {"entities" : qUnion([Q0, Q1, Q2, Q3, Q4, Q5]), "radius" : 3 * mm, "tangentPropagation" : true, "allowEdgeOverflow" : false});
        }
        {
            var Q0;
            Q0=makeQuery(id+"F1.opExtrude","CAP_EDGE",EDGE,{"disambiguationData":[OSD([sQuery(id+"F0.wireOp",EDGE,"E1.bottom")])],"isStart":false});
            fillet(context, id + "F15", {"entities" : qUnion([Q0]), "radius" : 2 * mm, "tangentPropagation" : true, "allowEdgeOverflow" : false});
        }
        {
            var Q0;
            {var subQ0=sQuery(id+"F0.wireOp",EDGE,"E21.filletArc");var subQ1=sQuery(id+"F0.wireOp",EDGE,"E7");var subQ2=sQuery(id+"F0.wireOp",EDGE,"E6");var subQ3=sQuery(id+"F0.wireOp",EDGE,"E5");var subQ4=sQuery(id+"F0.wireOp",EDGE,"E4");var subQ5=sQuery(id+"F0.wireOp",EDGE,"E22.filletArc");var subQ6=sQuery(id+"F0.wireOp",EDGE,"E1.bottom");var subQ7=sQuery(id+"F0.wireOp",EDGE,"E1.right");var subQ8=sQuery(id+"F0.wireOp",EDGE,"E1.top");var subQ9=sQuery(id+"F0.wireOp",EDGE,"E1.left");var subQ10=sQuery(id+"F0.wireOp",EDGE,"E23.filletArc");var subQ11=sQuery(id+"F0.wireOp",EDGE,"E24.filletArc");Q0=makeQuery(id+"F2.boolean.opBoolean","SPLIT",FACE,{"disambiguationData":[TD([makeQuery(id+"F1.opExtrude","SWEPT_FACE",FACE,{"disambiguationData":[OSD([subQ6])]})])],"derivedFrom":makeQuery(id+"F1.opExtrude","CAP_FACE",FACE,{"disambiguationData":[OSD([subQ6,subQ8,subQ9,subQ7,subQ4,subQ3,subQ2,subQ1,subQ0,subQ5,subQ10,subQ11])],"isStart":true})});}
            var sketch = newSketch(context, id + "F16", { "sketchPlane" : qUnion([Q0])});
            skLineSegment(sketch, "E79", {"start": v(0, 74.25) * mm, "end": v(0, 104.25) * mm, "construction": true});
            skCircle(sketch, "E80", {"center": v(0, 104.25) * mm, "radius": 6 * mm});
            skLineSegment(sketch, "E81", {"start": v(-15, 92.25) * mm, "end": v(-15, 104.25) * mm});
            skLineSegment(sketch, "E82", {"start": v(15, 92.25) * mm, "end": v(15, 104.25) * mm});
            skArc(sketch, "E83", {"start": v(15, 104.25) * mm, "mid": v(0, 119.25) * mm, "end": v(-15, 104.25) * mm});
            skLineSegment(sketch, "E84", {"start": v(15, 92.25) * mm, "end": v(33, 74.25) * mm});
            skLineSegment(sketch, "E85", {"start": v(-15, 92.25) * mm, "end": v(-36.2, 74.25) * mm});
            skLineSegment(sketch, "E86", {"start": v(-74.25, 0) * mm, "end": v(74.25, 0) * mm, "construction": true});
            skLineSegment(sketch, "E87.MirrorCS", {"start": v(-15, -92.25) * mm, "end": v(-15, -104.25) * mm});
            skLineSegment(sketch, "E88.MirrorCS", {"start": v(15, -92.25) * mm, "end": v(15, -104.25) * mm});
            skCircle(sketch, "E89.MirrorC", {"center": v(0, -104.25) * mm, "radius": 6 * mm});
            skLineSegment(sketch, "E90.MirrorCS", {"start": v(0, -74.25) * mm, "end": v(0, -104.25) * mm, "construction": true});
            skArc(sketch, "E91.MirrorCS", {"start": v(15, -104.25) * mm, "mid": v(0, -119.25) * mm, "end": v(-15, -104.25) * mm});
            skLineSegment(sketch, "E92.MirrorCS", {"start": v(15, -92.25) * mm, "end": v(33, -74.25) * mm});
            skLineSegment(sketch, "E93.MirrorCS", {"start": v(-15, -92.25) * mm, "end": v(-36.2, -74.25) * mm});
            skSolve(sketch);
        }
        {
            var Q0;
            Q0=makeQuery(id+"F16.imprint","IMPRINT",FACE,{"disambiguationData":[TD([[makeQuery(id+"F16.imprint","IMPRINT",EDGE,{"derivedFrom":sQuery(id+"F16.wireOp",EDGE,"E80")}),-1.0]])]});
            var Q1;
            Q1=makeQuery(id+"F16.imprint","IMPRINT",FACE,{"disambiguationData":[TD([[makeQuery(id+"F16.imprint","IMPRINT",EDGE,{"derivedFrom":sQuery(id+"F16.wireOp",EDGE,"E87.MirrorCS")}),1.0]])]});
            var Q2;
            Q2=makeQuery(id+"F16.imprint","IMPRINT",FACE,{"disambiguationData":[TD([[makeQuery(id+"F16.imprint","IMPRINT",EDGE,{"derivedFrom":makeQuery(id+"F1.opExtrude","CAP_EDGE",EDGE,{"disambiguationData":[OSD([sQuery(id+"F0.wireOp",EDGE,"E1.left")])],"isStart":true})}),-1.0]])]});
            var Q3;
            Q3=makeQuery(id+"F2.opExtrude","CAP_FACE",FACE,{"disambiguationData":[OSD([sQuery(id+"F0.wireOp",EDGE,"E12"),sQuery(id+"F0.wireOp",EDGE,"E13"),sQuery(id+"F0.wireOp",EDGE,"E14"),sQuery(id+"F0.wireOp",EDGE,"E15"),sQuery(id+"F0.wireOp",EDGE,"E17.filletArc"),sQuery(id+"F0.wireOp",EDGE,"E18.filletArc"),sQuery(id+"F0.wireOp",EDGE,"E19.filletArc"),sQuery(id+"F0.wireOp",EDGE,"E20.filletArc"),sQuery(id+"F0.wireOp",EDGE,"E25.0"),sQuery(id+"F0.wireOp",EDGE,"E25.1"),sQuery(id+"F0.wireOp",EDGE,"E25.2"),sQuery(id+"F0.wireOp",EDGE,"E25.3"),sQuery(id+"F0.wireOp",EDGE,"E25.4"),sQuery(id+"F0.wireOp",EDGE,"E25.5"),sQuery(id+"F0.wireOp",EDGE,"E25.6"),sQuery(id+"F0.wireOp",EDGE,"E25.7")])],"isStart":false});
            extrude(context, id + "F17", {"entities" : qUnion([Q0, Q1, Q2]), "endBound" : BoundingType.UP_TO_SURFACE, "depth" : 25 * mm, "endBoundEntityFace" : qUnion([Q3]), "offsetDistance" : 25 * mm});
        }
    });
